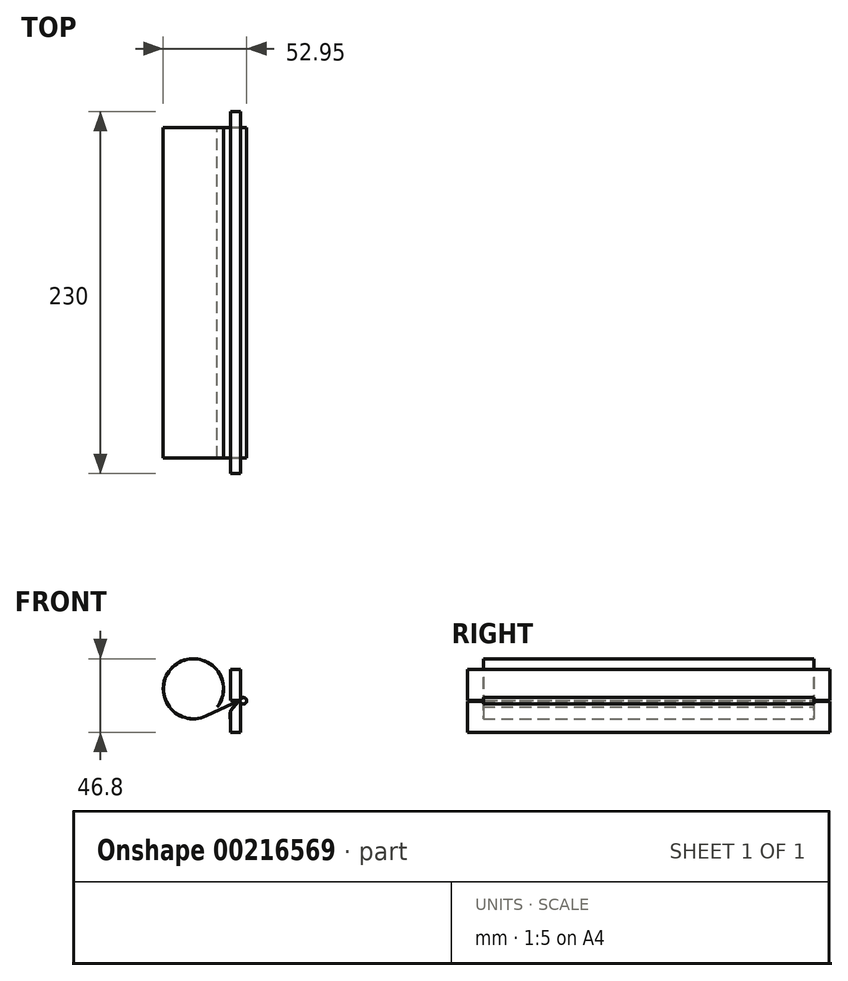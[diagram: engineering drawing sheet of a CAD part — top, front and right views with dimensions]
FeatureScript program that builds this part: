
annotation { "Feature Type Name" : "Feature", "Feature Type Description" : "" }
export const myFeature = defineFeature(function(context is Context, id is Id, definition is map)
    precondition{}
    {
        {
            var Q0;
            Q0=qCreatedBy(makeId("Front.planeOp"),FACE);
            var sketch = newSketch(context, id + "F0", { "sketchPlane" : qUnion([Q0])});
            skArc(sketch, "E0", {"start": v(0, 0.25) * mm, "mid": v(0.53, 0.47) * mm, "end": v(0.75, 1) * mm});
            skArc(sketch, "E1", {"start": v(0.75, -1) * mm, "mid": v(0.26, -0.3) * mm, "end": v(-0.57, -0.52) * mm, "construction": true});
            skCircle(sketch, "E2", {"center": v(2.64, 0) * mm, "radius": 2 * mm, "construction": true});
            skArc(sketch, "E3", {"start": v(0.7, -0.73) * mm, "mid": v(4.72, 0) * mm, "end": v(0.7, 0.73) * mm});
            skArc(sketch, "E4", {"start": v(0.35, 0.25) * mm, "mid": v(0.6, 0.44) * mm, "end": v(0.77, 0.7) * mm});
            skArc(sketch, "E5", {"start": v(0.77, -0.7) * mm, "mid": v(0.14, -0.19) * mm, "end": v(-0.63, -0.47) * mm});
            skLineSegment(sketch, "E6", {"start": v(0.75, -1) * mm, "end": v(0.75, -20.05) * mm, "construction": true});
            skLineSegment(sketch, "E7", {"start": v(-0.57, -0.52) * mm, "end": v(-5.13, -5.95) * mm, "construction": true});
            skLineSegment(sketch, "E8", {"start": v(-0.63, -0.47) * mm, "end": v(-5.2, -5.9) * mm});
            skLineSegment(sketch, "E9", {"start": v(0.35, 0.25) * mm, "end": v(-21.02, -9.71) * mm});
            skLineSegment(sketch, "E10", {"start": v(0.32, 0.32) * mm, "end": v(-21.05, -9.65) * mm});
            skLineSegment(sketch, "E11", {"start": v(-5.6, -7.23) * mm, "end": v(-5.6, -20.05) * mm, "construction": true});
            skLineSegment(sketch, "E12", {"start": v(-5.6, -20.05) * mm, "end": v(0.75, -20.05) * mm, "construction": true});
            skLineSegment(sketch, "E13", {"start": v(0, 0) * mm, "end": v(-7.46, 0) * mm, "construction": true});
            skLineSegment(sketch, "E14", {"start": v(0, 0.25) * mm, "end": v(-5.6, 0.25) * mm, "construction": true});
            skLineSegment(sketch, "E15", {"start": v(-5.6, 0.25) * mm, "end": v(-5.6, 20.05) * mm, "construction": true});
            skLineSegment(sketch, "E16", {"start": v(-5.6, 20.05) * mm, "end": v(0.75, 20.05) * mm, "construction": true});
            skLineSegment(sketch, "E17", {"start": v(0.75, 20.05) * mm, "end": v(0.75, 1) * mm, "construction": true});
            skLineSegment(sketch, "E18", {"start": v(-5.13, -5.95) * mm, "end": v(-0.57, -0.52) * mm});
            skArc(sketch, "E19", {"start": v(0.7, -0.73) * mm, "mid": v(0.13, -0.26) * mm, "end": v(-0.57, -0.52) * mm});
            skArc(sketch, "E20", {"start": v(0.77, -0.7) * mm, "mid": v(4.64, 0) * mm, "end": v(0.77, 0.7) * mm});
            skArc(sketch, "E21", {"start": v(-14, -4) * mm, "mid": v(-41.02, 22.48) * mm, "end": v(-21.05, -9.65) * mm, "construction": true});
            skArc(sketch, "E22", {"start": v(-13.94, -4.04) * mm, "mid": v(-41.07, 22.54) * mm, "end": v(-21.02, -9.71) * mm});
            skArc(sketch, "E23", {"start": v(-14, -4) * mm, "mid": v(-41.02, 22.48) * mm, "end": v(-21.05, -9.65) * mm});
            skLineSegment(sketch, "E24", {"start": v(-14, -4) * mm, "end": v(-13.94, -4.04) * mm});
            skArc(sketch, "E25", {"start": v(-5.13, -5.95) * mm, "mid": v(-5.48, -6.55) * mm, "end": v(-5.6, -7.23) * mm});
            skArc(sketch, "E26", {"start": v(-5.2, -5.9) * mm, "mid": v(-5.55, -6.52) * mm, "end": v(-5.68, -7.23) * mm});
            skLineSegment(sketch, "E27", {"start": v(-5.6, -11.37) * mm, "end": v(-5.6, -7.23) * mm});
            skLineSegment(sketch, "E28", {"start": v(-5.68, -7.23) * mm, "end": v(-5.68, -11.37) * mm});
            skLineSegment(sketch, "E29", {"start": v(-5.68, -11.37) * mm, "end": v(-5.6, -11.37) * mm});
            skSolve(sketch);
        }
        {
            var Q0;
            Q0 = qSketchRegion(id + "F0", true);
            extrude(context, id + "F1", {"entities" : qUnion([Q0]), "depth" : 210 * mm});
        }
        {
            var Q0;
            Q0=qCreatedBy(makeId("Front.planeOp"),FACE);
            var sketch = newSketch(context, id + "F2", { "sketchPlane" : qUnion([Q0])});
            skArc(sketch, "E30", {"start": v(0, 0.25) * mm, "mid": v(0.53, 0.47) * mm, "end": v(0.75, 1) * mm});
            skLineSegment(sketch, "E31", {"start": v(0.75, 20.05) * mm, "end": v(0.75, 1) * mm});
            skLineSegment(sketch, "E32", {"start": v(0.75, 20.05) * mm, "end": v(-5.6, 20.05) * mm});
            skLineSegment(sketch, "E33", {"start": v(-5.6, 20.05) * mm, "end": v(-5.6, 0.25) * mm});
            skLineSegment(sketch, "E34", {"start": v(-5.6, 0.25) * mm, "end": v(0, 0.25) * mm});
            skCircle(sketch, "E35", {"center": v(0, -1) * mm, "radius": 0.75 * mm});
            skLineSegment(sketch, "E36", {"start": v(-5.13, -5.95) * mm, "end": v(-0.57, -0.52) * mm});
            skLineSegment(sketch, "E37", {"start": v(0.75, -20.05) * mm, "end": v(0.75, -1) * mm});
            skLineSegment(sketch, "E38", {"start": v(0.75, -20.05) * mm, "end": v(-5.6, -20.05) * mm});
            skLineSegment(sketch, "E39", {"start": v(-5.6, -20.05) * mm, "end": v(-5.6, -7.23) * mm});
            skArc(sketch, "E40", {"start": v(-5.13, -5.95) * mm, "mid": v(-5.48, -6.55) * mm, "end": v(-5.6, -7.23) * mm});
            skSolve(sketch);
        }
        {
            var Q0;
            Q0 = qSketchRegion(id + "F2", true);
            extrude(context, id + "F3", {"entities" : qUnion([Q0]), "depth" : 220 * mm, "hasSecondDirection" : true, "secondDirectionOppositeDirection" : true, "secondDirectionDepth" : 10 * mm});
        }
    });
